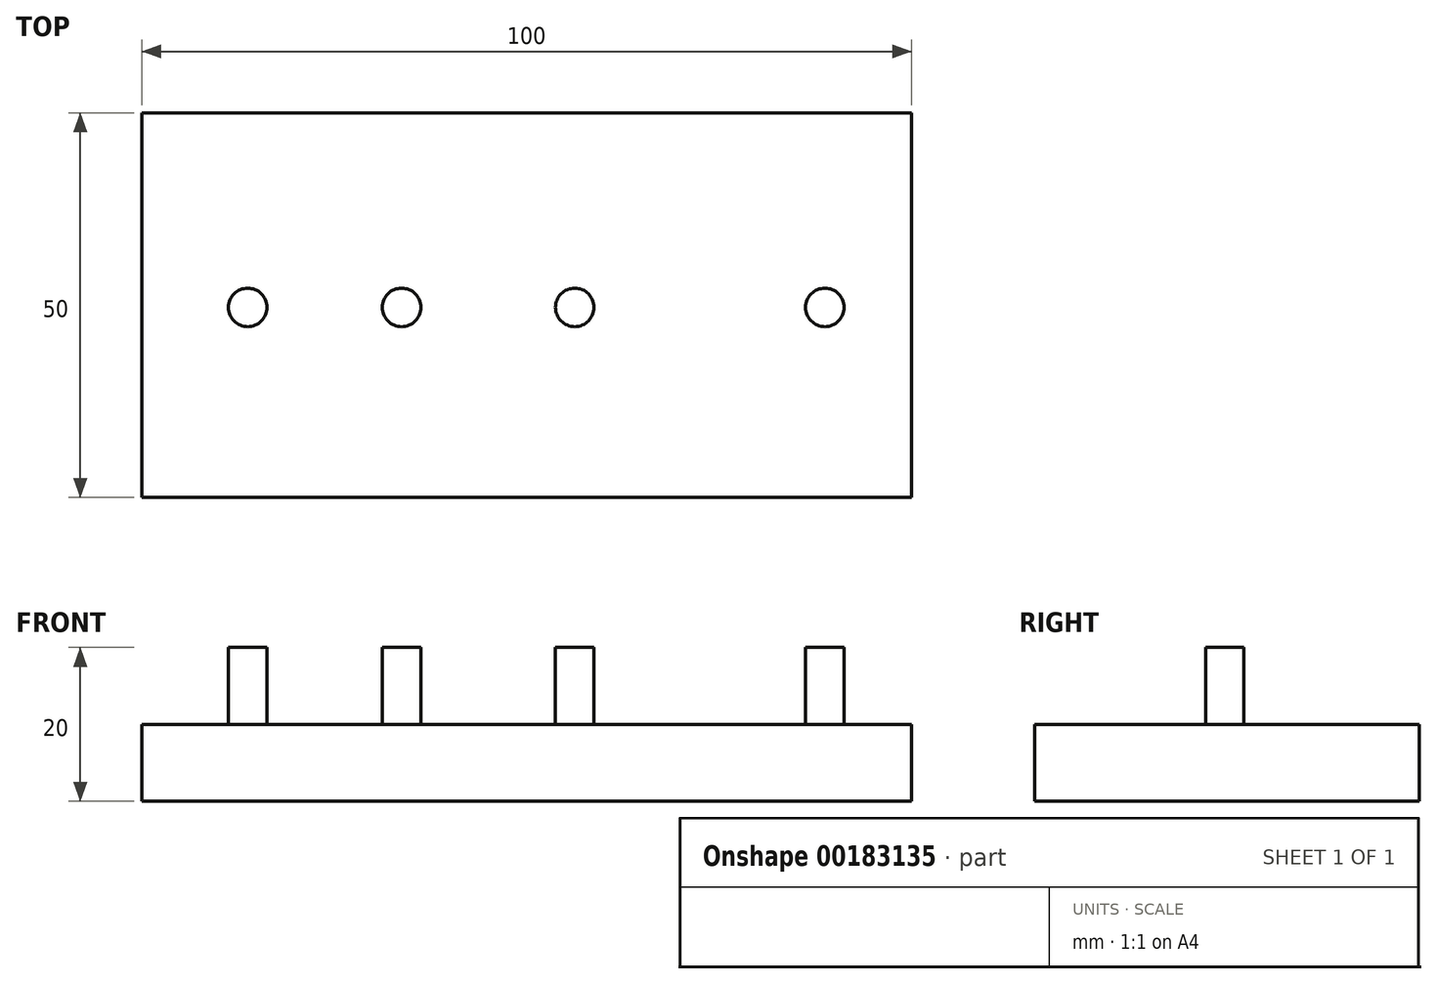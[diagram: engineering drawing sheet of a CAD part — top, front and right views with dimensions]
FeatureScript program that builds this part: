
annotation { "Feature Type Name" : "Feature", "Feature Type Description" : "" }
export const myFeature = defineFeature(function(context is Context, id is Id, definition is map)
    precondition{}
    {
        {
            var Q0;
            Q0=qCreatedBy(makeId("Top.planeOp"),FACE);
            var sketch = newSketch(context, id + "F0", { "sketchPlane" : qUnion([Q0])});
            skLineSegment(sketch, "E0.bottom", {"start": v(-50.7, 16.29) * mm, "end": v(49.3, 16.29) * mm});
            skLineSegment(sketch, "E0.top", {"start": v(-50.7, -33.71) * mm, "end": v(49.3, -33.71) * mm});
            skLineSegment(sketch, "E0.left", {"start": v(-50.7, 16.29) * mm, "end": v(-50.7, -33.71) * mm});
            skLineSegment(sketch, "E0.right", {"start": v(49.3, 16.29) * mm, "end": v(49.3, -33.71) * mm});
            skSolve(sketch);
        }
        {
            var Q0;
            Q0=makeQuery(id+"F0.imprint","IMPRINT",FACE,{"disambiguationData":[TD([[makeQuery(id+"F0.imprint","IMPRINT",EDGE,{"derivedFrom":sQuery(id+"F0.wireOp",EDGE,"E0.bottom")}),-1.0]])]});
            extrude(context, id + "F1", {"entities" : qUnion([Q0]), "depth" : 10 * mm});
        }
        {
            var Q0;
            Q0=makeQuery(id+"F1.opExtrude","CAP_FACE",FACE,{"disambiguationData":[OSD([sQuery(id+"F0.wireOp",EDGE,"E0.bottom"),sQuery(id+"F0.wireOp",EDGE,"E0.top"),sQuery(id+"F0.wireOp",EDGE,"E0.left"),sQuery(id+"F0.wireOp",EDGE,"E0.right")])],"isStart":false});
            var sketch = newSketch(context, id + "F2", { "sketchPlane" : qUnion([Q0])});
            skSolve(sketch);
        }
        {
            var Q0;
            Q0=makeQuery(id+"F2.imprint","IMPRINT",FACE,{"disambiguationData":[TD([[makeQuery(id+"F2.imprint","IMPRINT",EDGE,{"derivedFrom":makeQuery(id+"F1.opExtrude","CAP_EDGE",EDGE,{"disambiguationData":[OSD([sQuery(id+"F0.wireOp",EDGE,"E0.bottom")])],"isStart":false})}),-1.0]])]});
            var sketch = newSketch(context, id + "F3", { "sketchPlane" : qUnion([Q0])});
            skCircle(sketch, "E1", {"center": v(-36.94, -9) * mm, "radius": 2.5 * mm});
            skCircle(sketch, "E2", {"center": v(-16.94, -9) * mm, "radius": 2.5 * mm});
            skCircle(sketch, "E3", {"center": v(5.56, -9) * mm, "radius": 2.5 * mm});
            skCircle(sketch, "E4", {"center": v(38.06, -9) * mm, "radius": 2.5 * mm});
            skSolve(sketch);
        }
        {
            var Q0;
            Q0 = qSketchRegion(id + "F3", true);
            extrude(context, id + "F4", {"entities" : qUnion([Q0]), "operationType" : NewBodyOperationType.ADD, "depth" : 10 * mm});
        }
    });
